# Revit family: P200921MX-036c_MGC7536DS
name_source: partatom
category: Specialty Equipment
units: mm (PartAtom-declared; Revit-internal decimal feet)

## family parameters
Always vertical = Yes
Cut with Voids When Loaded = No
Enable Cutting in Views = No
Maintain Annotation Orientation = No
Part Type = Normal
Room Calculation Point = No
Round Connector Dimension = Use Diameter
Shared = No
Work Plane-Based = No

## types (1)
- MGC7536DS
    Accent Material = ARCAT - Metal - Steel - Black
    Amps = 15 A
    Body Material = ARCAT - Metal - Steel - Stainless
    Cooking Grate Material = ARCAT - Metal - Cast Iron 1/4" Plate
    Default Elevation = 0"
    Depth = 21"
    Description = 36-inch Wide Gas Cooktop with Power™ Burner
Table de cuisson au gaz de 36 po munie de 5 brûleurs Power™
    Dimension Guide = http://access.whirlpool.com Guide&sku=MGC7536DS&language=EN
http://access.whirlpool.com Guide&sku=MGC7536DS&language=EN
    Family Name = Cooking
    Feature 1 = 15,000-BTU Power™ Burner
Brûleur Power™ de 15 000 BTU
    Feature 2 = Heavy-duty DuraClean™ continuous cast-iron grates
Grilles continues en fonte robuste DuraClean™
    Feature 3 = 10 Year Limited Parts Warranty
Garantie limitée de 10 ans sur les pièces des brûleurs et des grilles
    Height = 3 11/16"
    Installation-Fabrication = https://www.whirlpool.com
https://www.whirlpool.com
    Knob Material = ARCAT - Metal - Steel - Gray
    Manufacturer = Maytag
    Model = MGC7536DS
    Voltage = 0 V
    Width = 36"

## geometry (parser evidence)
native form markers: Sweep x6
no freeform markers — native parametric forms only
